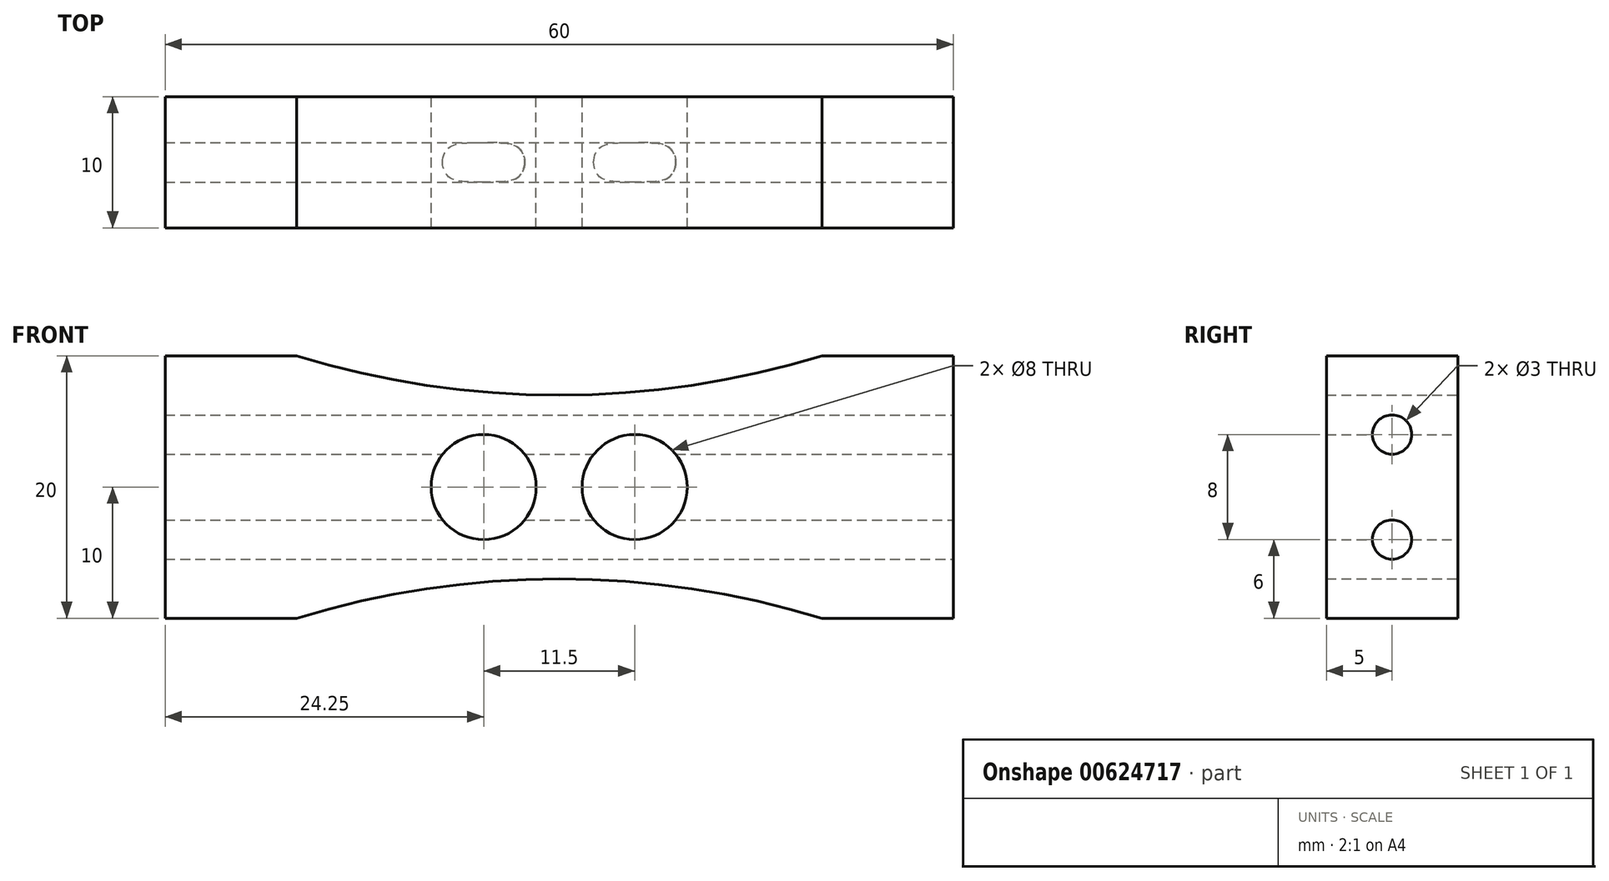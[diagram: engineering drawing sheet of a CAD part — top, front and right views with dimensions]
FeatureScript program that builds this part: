
annotation { "Feature Type Name" : "Feature", "Feature Type Description" : "" }
export const myFeature = defineFeature(function(context is Context, id is Id, definition is map)
    precondition{}
    {
        {
            var Q0;
            Q0=qCreatedBy(makeId("Front.planeOp"),FACE);
            var sketch = newSketch(context, id + "F0", { "sketchPlane" : qUnion([Q0])});
            skLineSegment(sketch, "E0.bottom", {"start": v(-30, -10) * mm, "end": v(-20, -10) * mm});
            skLineSegment(sketch, "E0.top", {"start": v(-30, 10) * mm, "end": v(-20, 10) * mm});
            skLineSegment(sketch, "E0.left", {"start": v(-30, -10) * mm, "end": v(-30, 10) * mm});
            skLineSegment(sketch, "E0.right", {"start": v(30, -10) * mm, "end": v(30, 10) * mm});
            skPoint(sketch, "E0.middle", {"position": v(0, 0) * mm});
            skLineSegment(sketch, "E1", {"start": v(-40.4, 0) * mm, "end": v(40.21, 0) * mm, "construction": true});
            skCircle(sketch, "E2", {"center": v(-5.75, 0) * mm, "radius": 4 * mm});
            skCircle(sketch, "E3", {"center": v(5.75, 0) * mm, "radius": 4 * mm});
            skArc(sketch, "E4", {"start": v(20, -10) * mm, "mid": v(0, -7) * mm, "end": v(-20, -10) * mm});
            skArc(sketch, "E5.MirrorCS", {"start": v(20, 10) * mm, "mid": v(0, 7) * mm, "end": v(-20, 10) * mm});
            skLineSegment(sketch, "E6.trimOffspring", {"start": v(20, -10) * mm, "end": v(30, -10) * mm});
            skLineSegment(sketch, "E7.trimOffspring", {"start": v(20, 10) * mm, "end": v(30, 10) * mm});
            skSolve(sketch);
        }
        {
            var Q0;
            Q0=makeQuery(id+"F0.imprint","IMPRINT",FACE,{"disambiguationData":[TD([[makeQuery(id+"F0.imprint","IMPRINT",EDGE,{"derivedFrom":sQuery(id+"F0.wireOp",EDGE,"E0.bottom")}),1.0]])]});
            extrude(context, id + "F1", {"entities" : qUnion([Q0]), "depth" : 10 * mm, "offsetDistance" : 25 * mm});
        }
        {
            var Q0;
            Q0=makeQuery(id+"F1.opExtrude","SWEPT_FACE",FACE,{"disambiguationData":[OSD([sQuery(id+"F0.wireOp",EDGE,"E0.right")])]});
            var sketch = newSketch(context, id + "F2", { "sketchPlane" : qUnion([Q0])});
            skLineSegment(sketch, "E8", {"start": v(-5, -10) * mm, "end": v(-5, 10) * mm, "construction": true});
            skCircle(sketch, "E9", {"center": v(-5, -4) * mm, "radius": 1.5 * mm});
            skCircle(sketch, "E10", {"center": v(-5, 4) * mm, "radius": 1.5 * mm});
            skLineSegment(sketch, "E11", {"start": v(-10, 0) * mm, "end": v(0, 0) * mm, "construction": true});
            skSolve(sketch);
        }
        {
            var Q0;
            Q0=makeQuery(id+"F2.imprint","IMPRINT",FACE,{"disambiguationData":[TD([[makeQuery(id+"F2.imprint","IMPRINT",EDGE,{"derivedFrom":sQuery(id+"F2.wireOp",EDGE,"E10")}),1.0]])]});
            var Q1;
            Q1=makeQuery(id+"F2.imprint","IMPRINT",FACE,{"disambiguationData":[TD([[makeQuery(id+"F2.imprint","IMPRINT",EDGE,{"derivedFrom":sQuery(id+"F2.wireOp",EDGE,"E9")}),1.0]])]});
            extrude(context, id + "F3", {"entities" : qUnion([Q0, Q1]), "operationType" : NewBodyOperationType.REMOVE, "oppositeDirection" : true, "depth" : 60 * mm, "offsetDistance" : 25 * mm});
        }
    });
